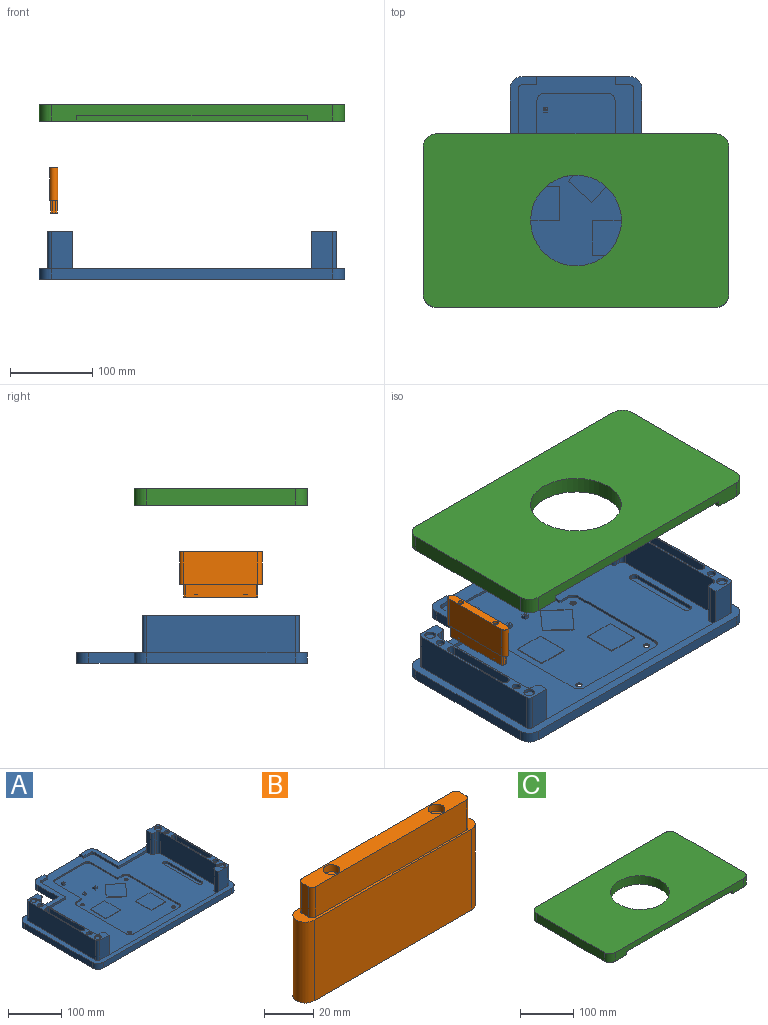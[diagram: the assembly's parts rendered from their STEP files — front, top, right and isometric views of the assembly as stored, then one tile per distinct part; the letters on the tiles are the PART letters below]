
ASSEMBLY  parts=3 mates=2
PART A: 197 faces, bbox 370x280x58 mm
  f0: plane 190x30mm, normal (0,0,1), area 1777.2mm2, adj f59,f60,f61,f62,f63,f64,f65,f66
  f1: plane 320x270mm, normal (0,0,1), area 39989mm2, adj f5,f6,f9,f21,f22,f23,f24,f25
  f2: plane 230x140mm, normal (0,0,1), area 23401.9mm2, adj f31,f32,f33,f34,f35,f36,f37,f38
  f3: plane 370x280mm, normal (0,0,-1), area 88037.7mm2, adj f7,f8,f9,f10,f11,f12,f13,f14
  f4: plane 190x30mm, normal (0,0,1), area 1777.2mm2, adj f45,f46,f47,f48,f49,f50,f51,f52
  f5: plane 75x5mm, normal (0,-1,0), area 375mm2, adj f1,f24,f30,f64
  f6: plane 290x5mm, normal (0,1,0), area 1450mm2, adj f1,f30,f50,f72
  f7: plane 55x13mm, normal (1,0,0), area 715mm2, adj f3,f8,f20,f30
  f8: cylinder r=15mm len=15mm, axis (0,0,-1), area 306.3mm2, adj f3,f7,f9,f30
  f9: plane 130x13mm, normal (0,1,0), area 1215mm2, adj f1,f3,f8,f10,f21,f29,f30
  f10: cylinder r=15mm len=15mm, axis (0,0,-1), area 306.3mm2, adj f3,f9,f11,f30
  f11: plane 55x13mm, normal (-1,0,0), area 715mm2, adj f3,f10,f12,f30
  f12: plane 90x13mm, normal (0,1,0), area 1170mm2, adj f3,f11,f13,f30
  f13: cylinder r=15mm len=15mm, axis (0,0,-1), area 306.3mm2, adj f3,f12,f14,f30
  f14: plane 180x13mm, normal (-1,0,0), area 2340mm2, adj f3,f13,f15,f30
  f15: cylinder r=15mm len=15mm, axis (0,0,-1), area 306.3mm2, adj f3,f14,f16,f30
  f16: plane 340x13mm, normal (0,-1,0), area 4420mm2, adj f3,f15,f17,f30
  f17: cylinder r=15mm len=15mm, axis (0,0,-1), area 306.3mm2, adj f3,f16,f18,f30
  f18: plane 180x13mm, normal (1,0,0), area 2340mm2, adj f3,f17,f19,f30
  f19: cylinder r=15mm len=15mm, axis (0,0,-1), area 306.3mm2, adj f3,f18,f20,f30
  f20: plane 90x13mm, normal (0,1,0), area 1170mm2, adj f3,f7,f19,f30
  f21: plane 10x5mm, normal (-1,0,0), area 50mm2, adj f1,f9,f22,f30
  f22: plane 17.5x5mm, normal (0,-1,0), area 87.5mm2, adj f1,f21,f23,f30
  f23: cylinder r=5mm len=5mm, axis (0,0,-1), area 39.3mm2, adj f1,f22,f24,f30
  f24: plane 65x5mm, normal (-1,0,0), area 325mm2, adj f1,f5,f23,f30
  f25: plane 75x5mm, normal (0,-1,0), area 375mm2, adj f1,f26,f30,f58
  f26: plane 65x5mm, normal (1,0,0), area 325mm2, adj f1,f25,f27,f30
  f27: cylinder r=5mm len=5mm, axis (0,0,-1), area 39.3mm2, adj f1,f26,f28,f30
  f28: plane 17.5x5mm, normal (0,-1,0), area 87.5mm2, adj f1,f27,f29,f30
  f29: plane 10x5mm, normal (1,0,0), area 50mm2, adj f1,f9,f28,f30
  f30: plane 370x280mm, normal (0,0,1), area 11392.5mm2, adj f5,f6,f7,f8,f9,f10,f11,f12
  f31: plane 70x3mm, normal (-1,0,0), area 210mm2, adj f1,f2,f32,f44
  f32: cylinder r=10mm len=10mm, axis (0,0,1), area 47.1mm2, adj f1,f2,f31,f33
  f33: plane 75x3mm, normal (0,-1,0), area 225mm2, adj f1,f2,f32,f34
  f34: cylinder r=10mm len=10mm, axis (0,0,1), area 47.1mm2, adj f1,f2,f33,f35
  f35: plane 70x3mm, normal (1,0,0), area 210mm2, adj f1,f2,f34,f36
  f36: plane 12.5x3mm, normal (0,-1,0), area 37.5mm2, adj f1,f2,f35,f37
  f37: cylinder r=10mm len=10mm, axis (0,0,1), area 47.1mm2, adj f1,f2,f36,f38
  f38: plane 130x3mm, normal (1,0,0), area 390mm2, adj f1,f2,f37,f39
  f39: cylinder r=10mm len=10mm, axis (0,0,1), area 47.1mm2, adj f1,f2,f38,f40
  f40: plane 120x3mm, normal (0,1,0), area 360mm2, adj f1,f2,f39,f41
  f41: cylinder r=10mm len=10mm, axis (0,0,1), area 47.1mm2, adj f1,f2,f40,f42
  f42: plane 130x3mm, normal (-1,0,0), area 390mm2, adj f1,f2,f41,f43
  f43: cylinder r=10mm len=10mm, axis (0,0,1), area 47.1mm2, adj f1,f2,f42,f44
  f44: plane 12.5x3mm, normal (0,-1,0), area 37.5mm2, adj f1,f2,f31,f43
  f45: plane 45x25mm, normal (0,-1,0), area 1125mm2, adj f4,f30,f49,f50
  f46: plane 180x45mm, normal (-1,0,0), area 8100mm2, adj f4,f30,f48,f49
  f47: plane 45x25mm, normal (0,1,0), area 1125mm2, adj f4,f30,f48,f58
  f48: cylinder r=5mm len=45mm, axis (0,0,-1), area 353.4mm2, adj f4,f30,f46,f47
  f49: cylinder r=5mm len=45mm, axis (0,0,-1), area 353.4mm2, adj f4,f30,f45,f46
  f50: plane 50x10mm, normal (1,0,0), area 500mm2, adj f1,f4,f6,f45,f51
  f51: cylinder r=5mm len=50mm, axis (0,0,-1), area 392.7mm2, adj f1,f4,f50,f52
  f52: plane 50x5mm, normal (0,1,0), area 250mm2, adj f1,f4,f51,f53
  f53: cylinder r=5mm len=50mm, axis (0,0,-1), area 392.7mm2, adj f1,f4,f52,f54
  f54: plane 150x50mm, normal (1,0,0), area 7500mm2, adj f1,f4,f53,f55
  f55: cylinder r=5mm len=50mm, axis (0,0,-1), area 392.7mm2, adj f1,f4,f54,f56
  f56: plane 50x5mm, normal (0,-1,0), area 250mm2, adj f1,f4,f55,f57
  f57: cylinder r=5mm len=50mm, axis (0,0,-1), area 392.7mm2, adj f1,f4,f56,f58
  f58: plane 50x10mm, normal (1,0,0), area 500mm2, adj f1,f4,f25,f47,f57
  f59: plane 45x25mm, normal (0,1,0), area 1125mm2, adj f0,f30,f63,f64
  f60: plane 180x45mm, normal (1,0,0), area 8100mm2, adj f0,f30,f62,f63
  f61: plane 45x25mm, normal (0,-1,0), area 1125mm2, adj f0,f30,f62,f72
  f62: cylinder r=5mm len=45mm, axis (0,0,-1), area 353.4mm2, adj f0,f30,f60,f61
  f63: cylinder r=5mm len=45mm, axis (0,0,-1), area 353.4mm2, adj f0,f30,f59,f60
  f64: plane 50x10mm, normal (-1,0,0), area 500mm2, adj f0,f1,f5,f59,f65
  f65: cylinder r=5mm len=50mm, axis (0,0,-1), area 392.7mm2, adj f0,f1,f64,f66
  f66: plane 50x5mm, normal (0,-1,0), area 250mm2, adj f0,f1,f65,f67
  f67: cylinder r=5mm len=50mm, axis (0,0,-1), area 392.7mm2, adj f0,f1,f66,f68
  f68: plane 150x50mm, normal (-1,0,0), area 7500mm2, adj f0,f1,f67,f69
  f69: cylinder r=5mm len=50mm, axis (0,0,-1), area 392.7mm2, adj f0,f1,f68,f70
  f70: plane 50x5mm, normal (0,1,0), area 250mm2, adj f0,f1,f69,f71
  f71: cylinder r=5mm len=50mm, axis (0,0,-1), area 392.7mm2, adj f0,f1,f70,f72
  f72: plane 50x10mm, normal (-1,0,0), area 500mm2, adj f0,f1,f6,f61,f71
  f73: cylinder r=6.5mm len=13mm, axis (0,0,1), area 142.9mm2, adj f0,f74
  f74: plane 13x13mm, normal (0,0,1), area 132.7mm2, adj f73
  f75: cylinder r=6.5mm len=13mm, axis (0,0,1), area 142.9mm2, adj f0,f76
  f76: plane 13x13mm, normal (0,0,1), area 132.7mm2, adj f75
  f77: cylinder r=6.5mm len=13mm, axis (0,0,1), area 142.9mm2, adj f4,f78
  f78: plane 13x13mm, normal (0,0,1), area 132.7mm2, adj f77
  f79: cylinder r=6.5mm len=13mm, axis (0,0,1), area 142.9mm2, adj f4,f80
  f80: plane 13x13mm, normal (0,0,1), area 132.7mm2, adj f79
  f81: cylinder r=5mm len=10mm, axis (0,0,1), area 157.1mm2, adj f0,f82
  f82: plane 10x10mm, normal (0,0,1), area 78.5mm2, adj f81
  f83: cylinder r=5mm len=10mm, axis (0,0,1), area 157.1mm2, adj f0,f84
  f84: plane 10x10mm, normal (0,0,1), area 78.5mm2, adj f83
  f85: cylinder r=5mm len=10mm, axis (0,0,1), area 157.1mm2, adj f4,f86
  f86: plane 10x10mm, normal (0,0,1), area 78.5mm2, adj f85
  f87: cylinder r=5mm len=10mm, axis (0,0,1), area 157.1mm2, adj f4,f88
  f88: plane 10x10mm, normal (0,0,1), area 78.5mm2, adj f87
  f89: cylinder r=3.75mm len=7.5mm, axis (0,0,1), area 47.1mm2, adj f2,f94
  f90: cylinder r=3.75mm len=7.5mm, axis (0,0,1), area 47.1mm2, adj f2,f93
  f91: cylinder r=3.75mm len=7.5mm, axis (0,0,1), area 47.1mm2, adj f2,f95
  f92: cylinder r=3.75mm len=7.5mm, axis (0,0,1), area 47.1mm2, adj f2,f96
  f93: cone r=6.75mm half-angle=45deg, axis (0,0,-1), area 140mm2, adj f3,f90
  f94: cone r=3.75mm half-angle=45deg, axis (0,0,-1), area 140mm2, adj f3,f89
  f95: cone r=3.75mm half-angle=45deg, axis (0,0,-1), area 140mm2, adj f3,f91
  f96: cone r=6.75mm half-angle=45deg, axis (0,0,-1), area 140mm2, adj f3,f92
  f97: cylinder r=5mm len=30mm, axis (0,0,1), area 235.6mm2, adj f4,f98,f104,f105
  f98: plane 91x30mm, normal (1,0,0), area 2730mm2, adj f4,f97,f99,f105
  f99: cylinder r=5mm len=30mm, axis (0,0,1), area 235.6mm2, adj f4,f98,f100,f105
  f100: plane 30x1mm, normal (0,1,0), area 30mm2, adj f4,f99,f101,f105
  f101: cylinder r=5mm len=30mm, axis (0,0,1), area 235.6mm2, adj f4,f100,f102,f105
  f102: plane 91x30mm, normal (-1,0,0), area 2730mm2, adj f4,f101,f103,f105
  f103: cylinder r=5mm len=30mm, axis (0,0,1), area 235.6mm2, adj f4,f102,f104,f105
  f104: plane 30x1mm, normal (0,-1,0), area 30mm2, adj f4,f97,f103,f105
  f105: plane 101x11mm, normal (0,0,1), area 274mm2, adj f97,f98,f99,f100,f101,f102,f103,f104
  f106: plane 6.85x6.85mm, normal (0,0,1), area 36.9mm2, adj f107
  f107: cylinder r=3.43mm len=6.85mm, axis (0,0,1), area 75.3mm2, adj f106,f108
  f108: plane 91x9mm, normal (0,0,1), area 741.9mm2, adj f107,f109,f110,f111,f112,f113,f114,f115
  f109: plane 87x15mm, normal (-1,0,0), area 1305mm2, adj f105,f108,f110,f114
  f110: cylinder r=2mm len=15mm, axis (0,0,1), area 47.1mm2, adj f105,f108,f109,f111
  f111: plane 15x5mm, normal (0,1,0), area 75mm2, adj f105,f108,f110,f112
  f112: cylinder r=2mm len=15mm, axis (0,0,1), area 47.1mm2, adj f105,f108,f111,f113
  f113: plane 87x15mm, normal (1,0,0), area 1305mm2, adj f105,f108,f112,f116
  f114: cylinder r=2mm len=15mm, axis (0,0,1), area 47.1mm2, adj f105,f108,f109,f115
  f115: plane 15x5mm, normal (0,-1,0), area 75mm2, adj f105,f108,f114,f116
  f116: cylinder r=2mm len=15mm, axis (0,0,1), area 47.1mm2, adj f105,f108,f113,f115
  f117: plane 6.85x6.85mm, normal (0,0,1), area 36.9mm2, adj f118
  f118: cylinder r=3.43mm len=6.85mm, axis (0,0,1), area 75.3mm2, adj f108,f117
  f119: plane 5.54x4mm, normal (1,0,0), area 22.2mm2, adj f2,f120,f123,f124
  f120: plane 6x4mm, normal (0,1,0), area 24mm2, adj f2,f119,f121,f124
  f121: plane 5.08x4mm, normal (-1,0,0), area 20.3mm2, adj f2,f120,f122,f124
  f122: plane 4x0.46mm, normal (-0.71,-0.71,0), area 2.6mm2, adj f2,f121,f123,f124
  f123: plane 5.54x4mm, normal (0,-1,0), area 22.2mm2, adj f2,f119,f122,f124
  f124: plane 6x5.54mm, normal (0,0,1), area 30mm2, adj f119,f120,f121,f122,f123,f195
  f125: plane 4.83x4mm, normal (1,0,0), area 19.3mm2, adj f2,f126,f129,f130
  f126: plane 6x4mm, normal (0,1,0), area 24mm2, adj f2,f125,f127,f130
  f127: plane 5.54x4mm, normal (-1,0,0), area 22.2mm2, adj f2,f126,f128,f130
  f128: plane 5.29x4mm, normal (0,-1,0), area 21.1mm2, adj f2,f127,f129,f130
  f129: plane 4x0.71mm, normal (0.71,-0.71,0), area 4mm2, adj f2,f125,f128,f130
  f130: plane 6x5.54mm, normal (0,0,1), area 29.8mm2, adj f125,f126,f127,f128,f129,f193
  f131: plane 6x4mm, normal (1,0,0), area 24mm2, adj f2,f132,f134,f135
  f132: plane 5.54x4mm, normal (0,1,0), area 22.2mm2, adj f2,f131,f133,f135
  f133: plane 6x4mm, normal (-1,0,0), area 24mm2, adj f2,f132,f134,f135
  f134: plane 5.54x4mm, normal (0,-1,0), area 22.2mm2, adj f2,f131,f133,f135
  f135: plane 6x5.54mm, normal (0,0,1), area 30.1mm2, adj f131,f132,f133,f134,f191
  f136: plane 38.5x1mm, normal (0,1,0), area 38.5mm2, adj f2,f137,f139,f140
  f137: plane 41.5x1mm, normal (-1,0,0), area 41.5mm2, adj f2,f136,f138,f140
  f138: plane 38.5x1mm, normal (0,-1,0), area 38.5mm2, adj f2,f137,f139,f140
  f139: plane 41.5x1mm, normal (1,0,0), area 41.5mm2, adj f2,f136,f138,f140
  f140: plane 41.5x38.5mm, normal (0,0,1), area 1597.8mm2, adj f136,f137,f138,f139
  f141: plane 38.5x1mm, normal (0,-1,0), area 38.5mm2, adj f2,f142,f144,f145
  f142: plane 41.5x1mm, normal (1,0,0), area 41.5mm2, adj f2,f141,f143,f145
  f143: plane 38.5x1mm, normal (0,1,0), area 38.5mm2, adj f2,f142,f144,f145
  f144: plane 41.5x1mm, normal (-1,0,0), area 41.5mm2, adj f2,f141,f143,f145
  f145: plane 41.5x38.5mm, normal (0,0,1), area 1597.8mm2, adj f141,f142,f143,f144
  f146: plane 30.93x27.67mm, normal (-0.75,0.67,0), area 41.5mm2, adj f2,f147,f149,f150
  f147: plane 28.7x25.67mm, normal (-0.67,-0.75,0), area 38.5mm2, adj f2,f146,f148,f150
  f148: plane 30.93x27.67mm, normal (0.75,-0.67,0), area 41.5mm2, adj f2,f147,f149,f150
  f149: plane 28.7x25.67mm, normal (0.67,0.75,0), area 38.5mm2, adj f2,f146,f148,f150
  f150: plane 56.6x56.36mm, normal (0,0,1), area 1597.7mm2, adj f146,f147,f148,f149
  f151: plane 5x1mm, normal (0,-1,0), area 5mm2, adj f1,f152,f158,f159
  f152: cylinder r=5mm len=5mm, axis (0,0,1), area 39.3mm2, adj f1,f151,f153,f159
  f153: plane 91x5mm, normal (1,0,0), area 455mm2, adj f1,f152,f154,f159
  f154: cylinder r=5mm len=5mm, axis (0,0,1), area 39.3mm2, adj f1,f153,f155,f159
  f155: plane 5x1mm, normal (0,1,0), area 5mm2, adj f1,f154,f156,f159
  f156: cylinder r=5mm len=5mm, axis (0,0,1), area 39.3mm2, adj f1,f155,f157,f159
  f157: plane 91x5mm, normal (-1,0,0), area 455mm2, adj f1,f156,f158,f159
  f158: cylinder r=5mm len=5mm, axis (0,0,1), area 39.3mm2, adj f1,f151,f157,f159
  f159: plane 101x11mm, normal (0,0,1), area 1089.5mm2, adj f151,f152,f153,f154,f155,f156,f157,f158
  f160: plane 5x1mm, normal (0,-1,0), area 5mm2, adj f1,f161,f167,f168
  f161: cylinder r=5mm len=5mm, axis (0,0,1), area 39.3mm2, adj f1,f160,f162,f168
  f162: plane 91x5mm, normal (1,0,0), area 455mm2, adj f1,f161,f163,f168
  f163: cylinder r=5mm len=5mm, axis (0,0,1), area 39.3mm2, adj f1,f162,f164,f168
  f164: plane 5x1mm, normal (0,1,0), area 5mm2, adj f1,f163,f165,f168
  f165: cylinder r=5mm len=5mm, axis (0,0,1), area 39.3mm2, adj f1,f164,f166,f168
  f166: plane 91x5mm, normal (-1,0,0), area 455mm2, adj f1,f165,f167,f168
  f167: cylinder r=5mm len=5mm, axis (0,0,1), area 39.3mm2, adj f1,f160,f166,f168
  f168: plane 101x11mm, normal (0,0,1), area 1089.5mm2, adj f160,f161,f162,f163,f164,f165,f166,f167
  f169: cylinder r=5mm len=30mm, axis (0,0,1), area 235.6mm2, adj f0,f170,f176,f177
  f170: plane 30x1mm, normal (0,-1,0), area 30mm2, adj f0,f169,f171,f177
  f171: cylinder r=5mm len=30mm, axis (0,0,1), area 235.6mm2, adj f0,f170,f172,f177
  f172: plane 91x30mm, normal (1,0,0), area 2730mm2, adj f0,f171,f173,f177
  f173: cylinder r=5mm len=30mm, axis (0,0,1), area 235.6mm2, adj f0,f172,f174,f177
  f174: plane 30x1mm, normal (0,1,0), area 30mm2, adj f0,f173,f175,f177
  f175: cylinder r=5mm len=30mm, axis (0,0,1), area 235.6mm2, adj f0,f174,f176,f177
  f176: plane 91x30mm, normal (-1,0,0), area 2730mm2, adj f0,f169,f175,f177
  f177: plane 101x11mm, normal (0,0,1), area 274mm2, adj f169,f170,f171,f172,f173,f174,f175,f176
  f178: plane 87x15mm, normal (-1,0,0), area 1305mm2, adj f177,f179,f183,f188
  f179: cylinder r=2mm len=15mm, axis (0,0,1), area 47.1mm2, adj f177,f178,f180,f183
  f180: plane 15x5mm, normal (0,-1,0), area 75mm2, adj f177,f179,f181,f183
  f181: cylinder r=2mm len=15mm, axis (0,0,1), area 47.1mm2, adj f177,f180,f182,f183
  f182: plane 87x15mm, normal (1,0,0), area 1305mm2, adj f177,f181,f183,f186
  f183: plane 91x9mm, normal (0,0,1), area 741.9mm2, adj f178,f179,f180,f181,f182,f185,f186,f187
  f184: plane 6.85x6.85mm, normal (0,0,1), area 36.9mm2, adj f185
  f185: cylinder r=3.43mm len=6.85mm, axis (0,0,1), area 75.3mm2, adj f183,f184
  f186: cylinder r=2mm len=15mm, axis (0,0,1), area 47.1mm2, adj f177,f182,f183,f187
  f187: plane 15x5mm, normal (0,1,0), area 75mm2, adj f177,f183,f186,f188
  f188: cylinder r=2mm len=15mm, axis (0,0,1), area 47.1mm2, adj f177,f178,f183,f187
  f189: plane 6.85x6.85mm, normal (0,0,1), area 36.9mm2, adj f190
  f190: cylinder r=3.43mm len=6.85mm, axis (0,0,1), area 75.3mm2, adj f183,f189
  f191: cylinder r=1mm len=5mm, axis (0,0,1), area 31.4mm2, adj f135,f192
  f192: plane 2x2mm, normal (0,0,1), area 3.1mm2, adj f191
  f193: cylinder r=1mm len=5mm, axis (0,0,1), area 31.4mm2, adj f130,f194
  f194: plane 2x2mm, normal (0,0,1), area 3.1mm2, adj f193
  f195: cylinder r=1mm len=5mm, axis (0,0,1), area 31.4mm2, adj f124,f196
  f196: plane 2x2mm, normal (0,0,1), area 3.1mm2, adj f195
PART B: 23 faces, bbox 100x10x55 mm
  f0: plane 100x10mm, normal (0,0,1), area 262mm2, adj f1,f2,f3,f4,f6,f7,f8,f9
  f1: plane 90x40mm, normal (0,1,0), area 3600mm2, adj f0,f2,f4,f5
  f2: cylinder r=5mm len=40mm, axis (0,0,-1), area 628.3mm2, adj f0,f1,f3,f5
  f3: plane 90x40mm, normal (0,-1,0), area 3600mm2, adj f0,f2,f4,f5
  f4: cylinder r=5mm len=40mm, axis (0,0,-1), area 628.3mm2, adj f0,f1,f3,f5
  f5: plane 100x10mm, normal (0,0,-1), area 904.8mm2, adj f1,f2,f3,f4,f15,f17
  f6: plane 86x15mm, normal (0,-1,0), area 1290mm2, adj f0,f7,f13,f14
  f7: cylinder r=2mm len=15mm, axis (0,0,-1), area 47.1mm2, adj f0,f6,f8,f14
  f8: plane 15x4mm, normal (1,0,0), area 60mm2, adj f0,f7,f9,f14
  f9: cylinder r=2mm len=15mm, axis (0,0,-1), area 47.1mm2, adj f0,f8,f10,f14
  f10: plane 86x15mm, normal (0,1,0), area 1290mm2, adj f0,f9,f11,f14
  f11: cylinder r=2mm len=15mm, axis (0,0,-1), area 47.1mm2, adj f0,f10,f12,f14
  f12: plane 15x4mm, normal (-1,0,0), area 60mm2, adj f0,f11,f13,f14
  f13: cylinder r=2mm len=15mm, axis (0,0,-1), area 47.1mm2, adj f0,f6,f12,f14
  f14: plane 90x8mm, normal (0,0,1), area 642.9mm2, adj f6,f7,f8,f9,f10,f11,f12,f13
  f15: cylinder r=3.43mm len=6.85mm, axis (0,0,-1), area 75.3mm2, adj f5,f16
  f16: plane 6.85x6.85mm, normal (0,0,-1), area 36.9mm2, adj f15
  f17: cylinder r=3.43mm len=6.85mm, axis (0,0,-1), area 75.3mm2, adj f5,f18
  f18: plane 6.85x6.85mm, normal (0,0,-1), area 36.9mm2, adj f17
  f19: cylinder r=3.43mm len=6.85mm, axis (0,0,1), area 75.3mm2, adj f14,f20
  f20: plane 6.85x6.85mm, normal (0,0,1), area 36.9mm2, adj f19
  f21: cylinder r=3.43mm len=6.85mm, axis (0,0,1), area 75.3mm2, adj f14,f22
  f22: plane 6.85x6.85mm, normal (0,0,1), area 36.9mm2, adj f21
PART C: 129 faces, bbox 370x210x20 mm
  f0: plane 192x32mm, normal (0,0,-1), area 2272.4mm2, adj f27,f28,f29,f30,f31,f32,f33,f34
  f1: plane 340x20mm, normal (0,-1,0), area 4840mm2, adj f2,f6,f7,f11,f85,f86,f87
  f2: plane 370x210mm, normal (0,0,-1), area 27079.7mm2, adj f1,f3,f4,f5,f6,f7,f8,f9
  f3: plane 340x20mm, normal (0,1,0), area 4840mm2, adj f2,f4,f10,f11,f81,f82,f83
  f4: cylinder r=15mm len=20mm, axis (0,0,-1), area 471.2mm2, adj f2,f3,f5,f11
  f5: plane 180x20mm, normal (-1,0,0), area 3600mm2, adj f2,f4,f6,f11
  f6: cylinder r=15mm len=20mm, axis (0,0,-1), area 471.2mm2, adj f1,f2,f5,f11
  f7: cylinder r=15mm len=20mm, axis (0,0,-1), area 471.2mm2, adj f1,f2,f8,f11
  f8: plane 180x20mm, normal (1,0,0), area 3600mm2, adj f2,f7,f10,f11
  f9: cylinder r=55mm len=110mm, axis (0,0,-1), area 6911.5mm2, adj f2,f11
  f10: cylinder r=15mm len=20mm, axis (0,0,-1), area 471.2mm2, adj f2,f3,f8,f11
  f11: plane 370x210mm, normal (0,0,1), area 68003.5mm2, adj f1,f3,f4,f5,f6,f7,f8,f9
  f12: cylinder r=5mm len=10mm, axis (0,0,-1), area 78.5mm2, adj f2,f13,f25,f26
  f13: plane 27x10mm, normal (0,1,0), area 270mm2, adj f2,f12,f14,f26
  f14: plane 12x10mm, normal (1,0,0), area 120mm2, adj f2,f13,f15,f26
  f15: cylinder r=5mm len=10mm, axis (0,0,-1), area 78.5mm2, adj f2,f14,f16,f26
  f16: plane 10x5mm, normal (0,-1,0), area 50mm2, adj f2,f15,f17,f26
  f17: cylinder r=5mm len=10mm, axis (0,0,-1), area 78.5mm2, adj f2,f16,f18,f26
  f18: plane 148x10mm, normal (1,0,0), area 1480mm2, adj f2,f17,f19,f26
  f19: cylinder r=5mm len=10mm, axis (0,0,-1), area 78.5mm2, adj f2,f18,f20,f26
  f20: plane 10x5mm, normal (0,1,0), area 50mm2, adj f2,f19,f21,f26
  f21: cylinder r=5mm len=10mm, axis (0,0,-1), area 78.5mm2, adj f2,f20,f22,f26
  f22: plane 12x10mm, normal (1,0,0), area 120mm2, adj f2,f21,f23,f26
  f23: plane 27x10mm, normal (0,-1,0), area 270mm2, adj f2,f22,f24,f26
  f24: cylinder r=5mm len=10mm, axis (0,0,-1), area 78.5mm2, adj f2,f23,f25,f26
  f25: plane 182x10mm, normal (-1,0,0), area 1820mm2, adj f2,f12,f24,f26
  f26: plane 192x32mm, normal (0,0,-1), area 3361.9mm2, adj f12,f13,f14,f15,f16,f17,f18,f19
  f27: plane 10x5mm, normal (0,1,0), area 50mm2, adj f0,f2,f28,f40
  f28: cylinder r=5mm len=10mm, axis (0,0,-1), area 78.5mm2, adj f0,f2,f27,f29
  f29: plane 148x10mm, normal (-1,0,0), area 1480mm2, adj f0,f2,f28,f30
  f30: cylinder r=5mm len=10mm, axis (0,0,-1), area 78.5mm2, adj f0,f2,f29,f31
  f31: plane 10x5mm, normal (0,-1,0), area 50mm2, adj f0,f2,f30,f32
  f32: cylinder r=5mm len=10mm, axis (0,0,-1), area 78.5mm2, adj f0,f2,f31,f33
  f33: plane 12x10mm, normal (-1,0,0), area 120mm2, adj f0,f2,f32,f34
  f34: plane 27x10mm, normal (0,1,0), area 270mm2, adj f0,f2,f33,f35
  f35: cylinder r=5mm len=10mm, axis (0,0,-1), area 78.5mm2, adj f0,f2,f34,f36
  f36: plane 182x10mm, normal (1,0,0), area 1820mm2, adj f0,f2,f35,f37
  f37: cylinder r=5mm len=10mm, axis (0,0,-1), area 78.5mm2, adj f0,f2,f36,f38
  f38: plane 27x10mm, normal (0,-1,0), area 270mm2, adj f0,f2,f37,f39
  f39: plane 12x10mm, normal (-1,0,0), area 120mm2, adj f0,f2,f38,f40
  f40: cylinder r=5mm len=10mm, axis (0,0,-1), area 78.5mm2, adj f0,f2,f27,f39
  f41: cylinder r=75mm len=38.84mm, axis (0,0,-1), area 469.5mm2, adj f2,f42,f44,f45
  f42: plane 135.3x10mm, normal (0,1,0), area 1353mm2, adj f2,f41,f43,f45
  f43: plane 25x10mm, normal (1,0,0), area 250mm2, adj f2,f42,f44,f45
  f44: plane 96.46x10mm, normal (0,-1,0), area 964.6mm2, adj f2,f41,f43,f45
  f45: plane 135.3x25mm, normal (0,0,-1), area 2784.2mm2, adj f41,f42,f43,f44
  f46: cylinder r=75mm len=38.84mm, axis (0,0,-1), area 469.5mm2, adj f2,f47,f49,f50
  f47: plane 96.46x10mm, normal (0,-1,0), area 964.6mm2, adj f2,f46,f48,f50
  f48: plane 25x10mm, normal (-1,0,0), area 250mm2, adj f2,f47,f49,f50
  f49: plane 135.3x10mm, normal (0,1,0), area 1353mm2, adj f2,f46,f48,f50
  f50: plane 135.3x25mm, normal (0,0,-1), area 2784.2mm2, adj f46,f47,f48,f49
  f51: cylinder r=75mm len=25mm, axis (0,0,-1), area 261mm2, adj f2,f52,f54,f55
  f52: plane 79.88x10mm, normal (0,-1,0), area 798.8mm2, adj f2,f51,f53,f55
  f53: plane 25x10mm, normal (-1,0,0), area 250mm2, adj f2,f52,f54,f55
  f54: plane 86.91x10mm, normal (0,1,0), area 869.1mm2, adj f2,f51,f53,f55
  f55: plane 86.91x25mm, normal (0,0,-1), area 2065.2mm2, adj f51,f52,f53,f54
  f56: cylinder r=75mm len=25mm, axis (0,0,-1), area 261mm2, adj f2,f57,f59,f60
  f57: plane 86.91x10mm, normal (0,-1,0), area 869.1mm2, adj f2,f56,f58,f60
  f58: plane 25x10mm, normal (-1,0,0), area 250mm2, adj f2,f57,f59,f60
  f59: plane 79.88x10mm, normal (0,1,0), area 798.8mm2, adj f2,f56,f58,f60
  f60: plane 86.91x25mm, normal (0,0,-1), area 2065.2mm2, adj f56,f57,f58,f59
  f61: cylinder r=75mm len=38.84mm, axis (0,0,-1), area 469.5mm2, adj f2,f62,f64,f65
  f62: plane 135.3x10mm, normal (0,-1,0), area 1353mm2, adj f2,f61,f63,f65
  f63: plane 25x10mm, normal (-1,0,0), area 250mm2, adj f2,f62,f64,f65
  f64: plane 96.46x10mm, normal (0,1,0), area 964.6mm2, adj f2,f61,f63,f65
  f65: plane 135.3x25mm, normal (0,0,-1), area 2784.2mm2, adj f61,f62,f63,f64
  f66: cylinder r=75mm len=38.84mm, axis (0,0,-1), area 469.5mm2, adj f2,f67,f69,f70
  f67: plane 96.46x10mm, normal (0,1,0), area 964.6mm2, adj f2,f66,f68,f70
  f68: plane 25x10mm, normal (1,0,0), area 250mm2, adj f2,f67,f69,f70
  f69: plane 135.3x10mm, normal (0,-1,0), area 1353mm2, adj f2,f66,f68,f70
  f70: plane 135.3x25mm, normal (0,0,-1), area 2784.2mm2, adj f66,f67,f68,f69
  f71: plane 25x10mm, normal (1,0,0), area 250mm2, adj f2,f72,f74,f75
  f72: plane 86.91x10mm, normal (0,-1,0), area 869.1mm2, adj f2,f71,f73,f75
  f73: cylinder r=75mm len=25mm, axis (0,0,-1), area 261mm2, adj f2,f72,f74,f75
  f74: plane 79.88x10mm, normal (0,1,0), area 798.8mm2, adj f2,f71,f73,f75
  f75: plane 86.91x25mm, normal (0,0,-1), area 2065.2mm2, adj f71,f72,f73,f74
  f76: cylinder r=75mm len=25mm, axis (0,0,-1), area 261mm2, adj f2,f77,f79,f80
  f77: plane 86.91x10mm, normal (0,1,0), area 869.1mm2, adj f2,f76,f78,f80
  f78: plane 25x10mm, normal (1,0,0), area 250mm2, adj f2,f77,f79,f80
  f79: plane 79.88x10mm, normal (0,-1,0), area 798.8mm2, adj f2,f76,f78,f80
  f80: plane 86.91x25mm, normal (0,0,-1), area 2065.2mm2, adj f76,f77,f78,f79
  f81: plane 25x7mm, normal (1,0,0), area 175mm2, adj f2,f3,f82,f84
  f82: plane 280x25mm, normal (0,0,-1), area 7000mm2, adj f3,f81,f83,f84
  f83: plane 25x7mm, normal (-1,0,0), area 175mm2, adj f2,f3,f82,f84
  f84: plane 280x7mm, normal (0,1,0), area 1960mm2, adj f2,f81,f82,f83
  f85: plane 25x7mm, normal (-1,0,0), area 175mm2, adj f1,f2,f86,f88
  f86: plane 280x25mm, normal (0,0,-1), area 7000mm2, adj f1,f85,f87,f88
  f87: plane 25x7mm, normal (1,0,0), area 175mm2, adj f1,f2,f86,f88
  f88: plane 280x7mm, normal (0,-1,0), area 1960mm2, adj f2,f85,f86,f87
  f89: cylinder r=4.65mm len=9.3mm, axis (0,0,1), area 116.9mm2, adj f0,f90
  f90: plane 9.3x9.3mm, normal (0,0,-1), area 67.9mm2, adj f89
  f91: cylinder r=4.65mm len=9.3mm, axis (0,0,1), area 116.9mm2, adj f0,f92
  f92: plane 9.3x9.3mm, normal (0,0,-1), area 67.9mm2, adj f91
  f93: cylinder r=4.65mm len=9.3mm, axis (0,0,1), area 116.9mm2, adj f26,f94
  f94: plane 9.3x9.3mm, normal (0,0,-1), area 67.9mm2, adj f93
  f95: cylinder r=4.65mm len=9.3mm, axis (0,0,1), area 116.9mm2, adj f26,f96
  f96: plane 9.3x9.3mm, normal (0,0,-1), area 67.9mm2, adj f95
  f97: cylinder r=6.5mm len=13mm, axis (0,0,-1), area 142.9mm2, adj f0,f98
  f98: plane 13x13mm, normal (0,0,-1), area 132.7mm2, adj f97
  f99: cylinder r=6.5mm len=13mm, axis (0,0,-1), area 142.9mm2, adj f0,f100
  f100: plane 13x13mm, normal (0,0,-1), area 132.7mm2, adj f99
  f101: cylinder r=6.5mm len=13mm, axis (0,0,-1), area 142.9mm2, adj f26,f102
  f102: plane 13x13mm, normal (0,0,-1), area 132.7mm2, adj f101
  f103: cylinder r=6.5mm len=13mm, axis (0,0,-1), area 142.9mm2, adj f26,f104
  f104: plane 13x13mm, normal (0,0,-1), area 132.7mm2, adj f103
  f105: plane 1x1mm, normal (0,-1,0), area 1mm2, adj f0,f106,f112,f113
  f106: cylinder r=5mm len=5mm, axis (0,0,-1), area 7.9mm2, adj f0,f105,f107,f113
  f107: plane 91x1mm, normal (-1,0,0), area 91mm2, adj f0,f106,f108,f113
  f108: cylinder r=5mm len=5mm, axis (0,0,-1), area 7.9mm2, adj f0,f107,f109,f113
  f109: plane 1x1mm, normal (0,1,0), area 1mm2, adj f0,f108,f110,f113
  f110: cylinder r=5mm len=5mm, axis (0,0,-1), area 7.9mm2, adj f0,f109,f111,f113
  f111: plane 91x1mm, normal (1,0,0), area 91mm2, adj f0,f110,f112,f113
  f112: cylinder r=5mm len=5mm, axis (0,0,-1), area 7.9mm2, adj f0,f105,f111,f113
  f113: plane 101x11mm, normal (0,0,-1), area 274mm2, adj f105,f106,f107,f108,f109,f110,f111,f112
  f114: plane 91x9mm, normal (0,0,-1), area 815.6mm2, adj f115,f116,f117,f118,f119,f120,f121,f122
  f115: plane 87x1mm, normal (1,0,0), area 87mm2, adj f113,f114,f116,f122
  f116: cylinder r=2mm len=2mm, axis (0,0,-1), area 3.1mm2, adj f113,f114,f115,f117
  f117: plane 5x1mm, normal (0,1,0), area 5mm2, adj f113,f114,f116,f118
  f118: cylinder r=2mm len=2mm, axis (0,0,-1), area 3.1mm2, adj f113,f114,f117,f119
  f119: plane 87x1mm, normal (-1,0,0), area 87mm2, adj f113,f114,f118,f120
  f120: cylinder r=2mm len=2mm, axis (0,0,-1), area 3.1mm2, adj f113,f114,f119,f121
  f121: plane 5x1mm, normal (0,-1,0), area 5mm2, adj f113,f114,f120,f122
  f122: cylinder r=2mm len=2mm, axis (0,0,-1), area 3.1mm2, adj f113,f114,f115,f121
  f123: plane 6.85x6.85mm, normal (0,0,1), area 36.9mm2, adj f125
  f124: plane 6.85x6.85mm, normal (0,0,-1), area 36.9mm2, adj f125
  f125: cylinder r=3.43mm len=6.85mm, axis (0,0,-1), area 64.6mm2, adj f123,f124
  f126: plane 6.85x6.85mm, normal (0,0,1), area 36.9mm2, adj f128
  f127: plane 6.85x6.85mm, normal (0,0,-1), area 36.9mm2, adj f128
  f128: cylinder r=3.43mm len=6.85mm, axis (0,0,-1), area 64.6mm2, adj f126,f127
PLACE A t=(79.54,-37.17,-35.23)mm
PLACE B rot(axis=(0.71,0.71,0),180deg) t=(-87.96,-37.17,100.21)mm
PLACE C rot(axis=(-0.61,-0.67,-0.43),0deg) t=(79.54,-37.17,156.66)mm
MATE slider C.f114 <-> B.f5  axis (0,0,-1) through (-87.96,-37.17,168.66)mm
MATE slider B.f14 <-> A.f108  axis (0,0,-1) through (-87.96,-37.17,45.21)mm
